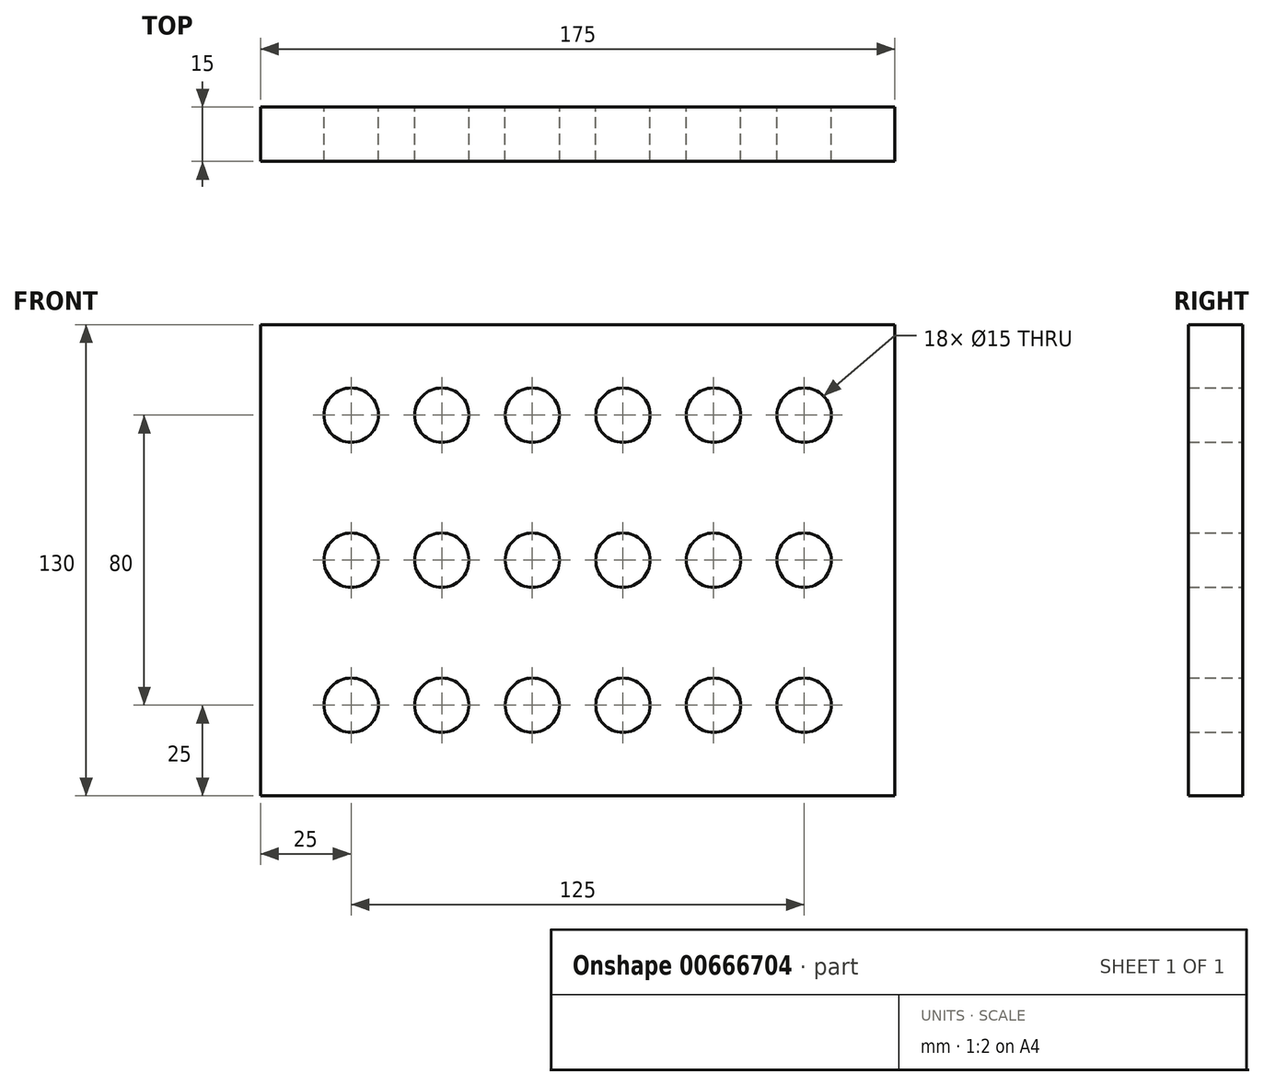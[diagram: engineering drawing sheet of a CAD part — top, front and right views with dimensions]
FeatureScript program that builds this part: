
annotation { "Feature Type Name" : "Feature", "Feature Type Description" : "" }
export const myFeature = defineFeature(function(context is Context, id is Id, definition is map)
    precondition{}
    {
        {
            var Q0;
            Q0=qCreatedBy(makeId("Front.planeOp"),FACE);
            var sketch = newSketch(context, id + "F0", { "sketchPlane" : qUnion([Q0])});
            skLineSegment(sketch, "E0.bottom", {"start": v(-87.5, 65) * mm, "end": v(87.5, 65) * mm});
            skLineSegment(sketch, "E0.top", {"start": v(-87.5, -65) * mm, "end": v(87.5, -65) * mm});
            skLineSegment(sketch, "E0.left", {"start": v(-87.5, 65) * mm, "end": v(-87.5, -65) * mm});
            skLineSegment(sketch, "E0.right", {"start": v(87.5, 65) * mm, "end": v(87.5, -65) * mm});
            skPoint(sketch, "E0.middle", {"position": v(0, 0) * mm});
            skCircle(sketch, "E1", {"center": v(-62.5, 40) * mm, "radius": 7.5 * mm});
            skCircle(sketch, "E2.0.1.0", {"center": v(-62.5, 0) * mm, "radius": 7.5 * mm});
            skCircle(sketch, "E2.0.2.0", {"center": v(-62.5, -40) * mm, "radius": 7.5 * mm});
            skCircle(sketch, "E2.1.0.0", {"center": v(-37.5, 40) * mm, "radius": 7.5 * mm});
            skCircle(sketch, "E2.1.1.0", {"center": v(-37.5, 0) * mm, "radius": 7.5 * mm});
            skCircle(sketch, "E2.1.2.0", {"center": v(-37.5, -40) * mm, "radius": 7.5 * mm});
            skCircle(sketch, "E2.2.0.0", {"center": v(-12.5, 40) * mm, "radius": 7.5 * mm});
            skCircle(sketch, "E2.2.1.0", {"center": v(-12.5, 0) * mm, "radius": 7.5 * mm});
            skCircle(sketch, "E2.2.2.0", {"center": v(-12.5, -40) * mm, "radius": 7.5 * mm});
            skCircle(sketch, "E2.3.0.0", {"center": v(12.5, 40) * mm, "radius": 7.5 * mm});
            skCircle(sketch, "E2.3.1.0", {"center": v(12.5, 0) * mm, "radius": 7.5 * mm});
            skCircle(sketch, "E2.3.2.0", {"center": v(12.5, -40) * mm, "radius": 7.5 * mm});
            skCircle(sketch, "E2.4.0.0", {"center": v(37.5, 40) * mm, "radius": 7.5 * mm});
            skCircle(sketch, "E2.4.1.0", {"center": v(37.5, 0) * mm, "radius": 7.5 * mm});
            skCircle(sketch, "E2.4.2.0", {"center": v(37.5, -40) * mm, "radius": 7.5 * mm});
            skCircle(sketch, "E2.5.0.0", {"center": v(62.5, 40) * mm, "radius": 7.5 * mm});
            skCircle(sketch, "E2.5.1.0", {"center": v(62.5, 0) * mm, "radius": 7.5 * mm});
            skCircle(sketch, "E2.5.2.0", {"center": v(62.5, -40) * mm, "radius": 7.5 * mm});
            skLineSegment(sketch, "E2.direction1", {"start": v(-62.5, 40) * mm, "end": v(-37.5, 40) * mm, "construction": true});
            skLineSegment(sketch, "E2.direction2", {"start": v(-62.5, 40) * mm, "end": v(-62.5, 0) * mm, "construction": true});
            skSolve(sketch);
        }
        {
            var Q0;
            Q0=makeQuery(id+"F0.imprint","IMPRINT",FACE,{"disambiguationData":[TD([[makeQuery(id+"F0.imprint","IMPRINT",EDGE,{"derivedFrom":sQuery(id+"F0.wireOp",EDGE,"E0.bottom")}),-1.0]])]});
            extrude(context, id + "F1", {"entities" : qUnion([Q0]), "depth" : 15 * mm, "offsetDistance" : 25 * mm});
        }
    });
